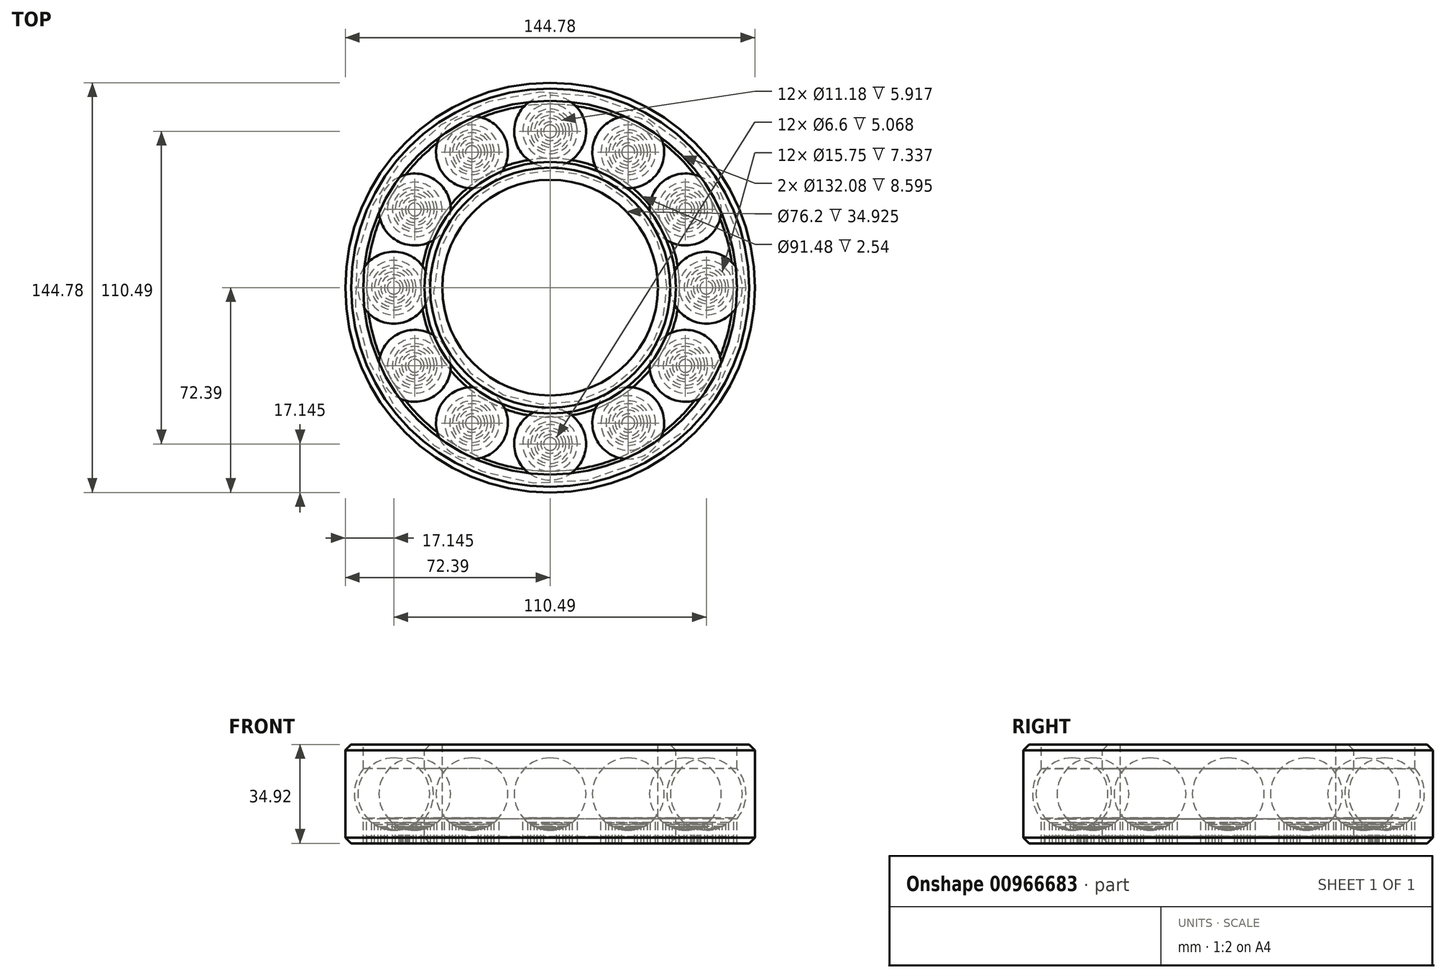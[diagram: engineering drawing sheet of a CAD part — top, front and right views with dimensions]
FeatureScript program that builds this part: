
annotation { "Feature Type Name" : "Feature", "Feature Type Description" : "" }
export const myFeature = defineFeature(function(context is Context, id is Id, definition is map)
    precondition{}
    {
        {
            var Q0;
            Q0=qCreatedBy(makeId("Front.planeOp"),FACE);
            var sketch = newSketch(context, id + "F0", { "sketchPlane" : qUnion([Q0])});
            skLineSegment(sketch, "E0", {"start": v(38.1, 17.46) * mm, "end": v(38.1, -17.46) * mm});
            skCircle(sketch, "E1", {"center": v(55.25, 0) * mm, "radius": 12.7 * mm, "construction": true});
            skArc(sketch, "E2", {"start": v(44.45, 8.87) * mm, "mid": v(41.27, 0) * mm, "end": v(44.45, -8.87) * mm});
            skLineSegment(sketch, "E3", {"start": v(72.4, 17.46) * mm, "end": v(72.4, -17.46) * mm});
            skLineSegment(sketch, "E4", {"start": v(38.1, 17.46) * mm, "end": v(44.45, 17.46) * mm});
            skLineSegment(sketch, "E5", {"start": v(44.45, 17.46) * mm, "end": v(44.45, 8.87) * mm});
            skLineSegment(sketch, "E6", {"start": v(38.1, -17.46) * mm, "end": v(44.45, -17.46) * mm});
            skLineSegment(sketch, "E7", {"start": v(44.45, -17.46) * mm, "end": v(44.45, -8.87) * mm});
            skLineSegment(sketch, "E8", {"start": v(72.4, 17.46) * mm, "end": v(66.04, 17.46) * mm});
            skLineSegment(sketch, "E9", {"start": v(66.04, 17.46) * mm, "end": v(66.04, 8.87) * mm});
            skLineSegment(sketch, "E10", {"start": v(72.4, -17.46) * mm, "end": v(66.04, -17.46) * mm});
            skLineSegment(sketch, "E11", {"start": v(66.04, -17.46) * mm, "end": v(66.04, -8.87) * mm});
            skArc(sketch, "E12.trimOffspring", {"start": v(66.04, -8.87) * mm, "mid": v(69.22, 0) * mm, "end": v(66.04, 8.87) * mm});
            skLineSegment(sketch, "E13", {"start": v(55.31, -12.7) * mm, "end": v(47.08, -12.7) * mm, "construction": true});
            skSolve(sketch);
        }
        {
            var Q0;
            Q0=qCreatedBy(makeId("Front.planeOp"),FACE);
            var sketch = newSketch(context, id + "F1", { "sketchPlane" : qUnion([Q0])});
            skLineSegment(sketch, "E14", {"start": v(0, 42.2) * mm, "end": v(0, -30.41) * mm});
            skSolve(sketch);
        }
        {
            var Q0;
            Q0 = qSketchRegion(id + "F0", true);
            var Q1;
            Q1=sQuery(id+"F1.wireOp",EDGE,"E14");
            revolve(context, id + "F2", {"surfaceOperationType" : NewSurfaceOperationType.NEW, "entities" : qUnion([Q0]), "axis" : qUnion([Q1]), "revolveType" : RevolveType.FULL});
        }
        {
            var Q0;
            Q0=qCreatedBy(makeId("Front.planeOp"),FACE);
            var sketch = newSketch(context, id + "F3", { "sketchPlane" : qUnion([Q0])});
            skLineSegment(sketch, "E15", {"start": v(55.25, 12.7) * mm, "end": v(55.25, -12.45) * mm});
            skArc(sketch, "E16", {"start": v(55.25, 12.7) * mm, "mid": v(67.9, 1.15) * mm, "end": v(57.53, -12.5) * mm});
            skPoint(sketch, "E17.orphan", {"position": v(55.25, -12.7) * mm});
            skLineSegment(sketch, "E18", {"start": v(57.53, -12.62) * mm, "end": v(57.53, -17.46) * mm});
            skLineSegment(sketch, "E19", {"start": v(55.25, -12.45) * mm, "end": v(55.25, -12.7) * mm});
            skLineSegment(sketch, "E20", {"start": v(55.25, -17.46) * mm, "end": v(57.53, -17.46) * mm});
            skArc(sketch, "E21", {"start": v(57.53, -12.5) * mm, "mid": v(56.4, -12.65) * mm, "end": v(55.25, -12.7) * mm});
            skArc(sketch, "E22", {"start": v(55.25, -12.83) * mm, "mid": v(56.4, -12.78) * mm, "end": v(57.53, -12.62) * mm});
            skLineSegment(sketch, "E23.trimOffspring", {"start": v(55.25, -12.83) * mm, "end": v(55.25, -17.46) * mm});
            skArc(sketch, "E24", {"start": v(58.55, -12.4) * mm, "mid": v(59.19, -12.2) * mm, "end": v(59.82, -11.98) * mm});
            skLineSegment(sketch, "E25", {"start": v(58.55, -12.4) * mm, "end": v(58.55, -17.46) * mm});
            skLineSegment(sketch, "E26", {"start": v(58.55, -17.46) * mm, "end": v(59.82, -17.46) * mm});
            skLineSegment(sketch, "E27", {"start": v(59.82, -17.46) * mm, "end": v(59.82, -11.98) * mm});
            skArc(sketch, "E28", {"start": v(60.83, -11.55) * mm, "mid": v(61.48, -11.21) * mm, "end": v(62.1, -10.84) * mm});
            skLineSegment(sketch, "E29", {"start": v(60.83, -11.55) * mm, "end": v(60.83, -17.46) * mm});
            skLineSegment(sketch, "E30", {"start": v(60.83, -17.46) * mm, "end": v(62.1, -17.46) * mm});
            skLineSegment(sketch, "E31", {"start": v(62.1, -17.46) * mm, "end": v(62.1, -10.84) * mm});
            skArc(sketch, "E32", {"start": v(63.12, -10.13) * mm, "mid": v(64.05, -9.33) * mm, "end": v(64.9, -8.45) * mm});
            skLineSegment(sketch, "E33", {"start": v(63.12, -10.13) * mm, "end": v(63.12, -17.46) * mm});
            skLineSegment(sketch, "E34", {"start": v(63.12, -17.46) * mm, "end": v(64.9, -17.46) * mm});
            skLineSegment(sketch, "E35", {"start": v(64.9, -17.46) * mm, "end": v(64.9, -8.45) * mm});
            skSolve(sketch);
        }
        {
            var Q0;
            Q0=qCreatedBy(makeId("Front.planeOp"),FACE);
            var sketch = newSketch(context, id + "F4", { "sketchPlane" : qUnion([Q0])});
            skLineSegment(sketch, "E36", {"start": v(55.25, 25) * mm, "end": v(55.25, -25.66) * mm});
            skSolve(sketch);
        }
        {
            var Q0;
            Q0 = qSketchRegion(id + "F3", true);
            var Q1;
            Q1=sQuery(id+"F4.wireOp",EDGE,"E36");
            revolve(context, id + "F5", {"surfaceOperationType" : NewSurfaceOperationType.NEW, "entities" : qUnion([Q0]), "axis" : qUnion([Q1]), "revolveType" : RevolveType.FULL});
        }
        {
            var Q0;
            Q0=makeQuery(id+"F5.opRevolve","SWEPT_BODY",BODY,{"disambiguationData":[OSD([sQuery(id+"F3.wireOp",EDGE,"E15"),sQuery(id+"F3.wireOp",EDGE,"E16"),sQuery(id+"F3.wireOp",EDGE,"E18"),sQuery(id+"F3.wireOp",EDGE,"E19"),sQuery(id+"F3.wireOp",EDGE,"E20")])]});
            var Q1;
            Q1=makeQuery(id+"F5.opRevolve","SWEPT_BODY",BODY,{"disambiguationData":[OSD([sQuery(id+"F3.wireOp",EDGE,"E32"),sQuery(id+"F3.wireOp",EDGE,"E33"),sQuery(id+"F3.wireOp",EDGE,"E34"),sQuery(id+"F3.wireOp",EDGE,"E35")])]});
            var Q2;
            Q2=makeQuery(id+"F5.opRevolve","SWEPT_BODY",BODY,{"disambiguationData":[OSD([sQuery(id+"F3.wireOp",EDGE,"E28"),sQuery(id+"F3.wireOp",EDGE,"E29"),sQuery(id+"F3.wireOp",EDGE,"E30"),sQuery(id+"F3.wireOp",EDGE,"E31")])]});
            var Q3;
            Q3=makeQuery(id+"F5.opRevolve","SWEPT_BODY",BODY,{"disambiguationData":[OSD([sQuery(id+"F3.wireOp",EDGE,"E24"),sQuery(id+"F3.wireOp",EDGE,"E25"),sQuery(id+"F3.wireOp",EDGE,"E26"),sQuery(id+"F3.wireOp",EDGE,"E27")])]});
            var Q4;
            Q4=makeQuery(id+"F5.opRevolve","SWEPT_BODY",BODY,{"disambiguationData":[OSD([sQuery(id+"F3.wireOp",EDGE,"E18"),sQuery(id+"F3.wireOp",EDGE,"E20"),sQuery(id+"F3.wireOp",EDGE,"E22"),sQuery(id+"F3.wireOp",EDGE,"E23.trimOffspring")])]});
            var Q5;
            Q5=sQuery(id+"F1.wireOp",EDGE,"E14");
            circularPattern(context, id + "F6", {"entities" : qUnion([Q0, Q1, Q2, Q3, Q4]), "axis" : qUnion([Q5]), "angle" : 360 * degree, "instanceCount" : 12, "equalSpace" : true});
        }
        {
            var Q0;
            Q0=makeQuery(id+"F2.opRevolve","SWEPT_EDGE",EDGE,{"disambiguationData":[OSD([sQuery(id+"F0.wireOp",EDGE,"E3"),sQuery(id+"F0.wireOp",EDGE,"E8")])]});
            var Q1;
            Q1=makeQuery(id+"F2.opRevolve","SWEPT_EDGE",EDGE,{"disambiguationData":[OSD([sQuery(id+"F0.wireOp",EDGE,"E3"),sQuery(id+"F0.wireOp",EDGE,"E10")])]});
            var Q2;
            Q2=makeQuery(id+"F2.opRevolve","SWEPT_EDGE",EDGE,{"disambiguationData":[OSD([sQuery(id+"F0.wireOp",EDGE,"E6"),sQuery(id+"F0.wireOp",EDGE,"E7")])]});
            var Q3;
            Q3=makeQuery(id+"F2.opRevolve","SWEPT_EDGE",EDGE,{"disambiguationData":[OSD([sQuery(id+"F0.wireOp",EDGE,"E4"),sQuery(id+"F0.wireOp",EDGE,"E5")])]});
            chamfer(context, id + "F7", {"entities" : qUnion([Q0, Q1, Q2, Q3]), "width" : 2.03 * mm, "tangentPropagation" : true});
        }
        {
            var Q0;
            Q0=makeQuery(id+"F2.opRevolve","SWEPT_FACE",FACE,{"disambiguationData":[OSD([sQuery(id+"F0.wireOp",EDGE,"E10")])]});
            var sketch = newSketch(context, id + "F8", { "sketchPlane" : qUnion([Q0])});
            skCircle(sketch, "E37", {"center": v(0, 0) * mm, "radius": 45.74 * mm});
            skCircle(sketch, "E38", {"center": v(0, 0) * mm, "radius": 64.82 * mm});
            skSolve(sketch);
        }
        {
            var Q0;
            Q0 = qSketchRegion(id + "F8", true);
            extrude(context, id + "F9", {"entities" : qUnion([Q0]), "oppositeDirection" : true, "depth" : 2.54 * mm, "offsetDistance" : 25.4 * mm});
        }
    });
